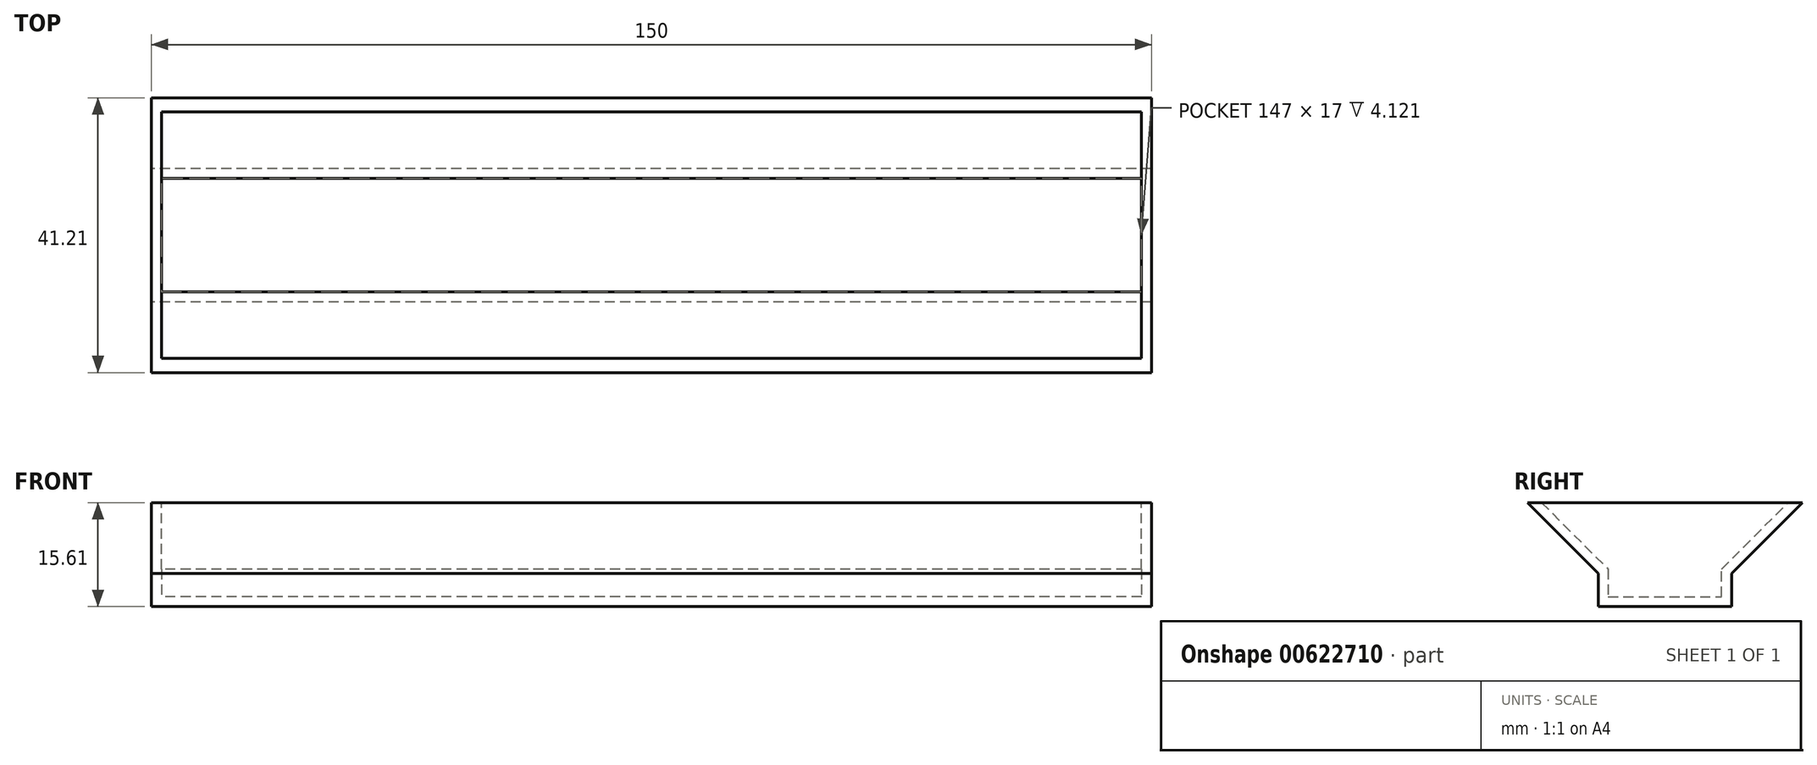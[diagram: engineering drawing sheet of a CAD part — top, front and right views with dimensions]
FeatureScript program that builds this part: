
annotation { "Feature Type Name" : "Feature", "Feature Type Description" : "" }
export const myFeature = defineFeature(function(context is Context, id is Id, definition is map)
    precondition{}
    {
        {
            var Q0;
            Q0=qCreatedBy(makeId("Right.planeOp"),FACE);
            var sketch = newSketch(context, id + "F0", { "sketchPlane" : qUnion([Q0])});
            skLineSegment(sketch, "E0", {"start": v(-10.24, 0) * mm, "end": v(9.76, 0) * mm});
            skLineSegment(sketch, "E1", {"start": v(9.76, 0) * mm, "end": v(9.76, 5) * mm});
            skLineSegment(sketch, "E2", {"start": v(9.76, 5) * mm, "end": v(20.36, 15.6) * mm});
            skLineSegment(sketch, "E3", {"start": v(20.36, 15.6) * mm, "end": v(-20.85, 15.6) * mm});
            skLineSegment(sketch, "E4", {"start": v(-20.85, 15.6) * mm, "end": v(-10.24, 5) * mm});
            skLineSegment(sketch, "E5", {"start": v(-10.24, 5) * mm, "end": v(-10.24, 0) * mm});
            skSolve(sketch);
        }
        {
            var Q0;
            Q0 = qSketchRegion(id + "F0", true);
            extrude(context, id + "F1", {"entities" : qUnion([Q0]), "endBound" : BoundingType.SYMMETRIC, "depth" : 150 * mm, "offsetDistance" : 25 * mm});
        }
        {
            var Q0;
            Q0=makeQuery(id+"F1.opExtrude","SWEPT_FACE",FACE,{"disambiguationData":[OSD([sQuery(id+"F0.wireOp",EDGE,"E3")])]});
            shell(context, id + "F2", {"entities" : qUnion([Q0]), "thickness" : 1.5 * mm});
        }
    });
